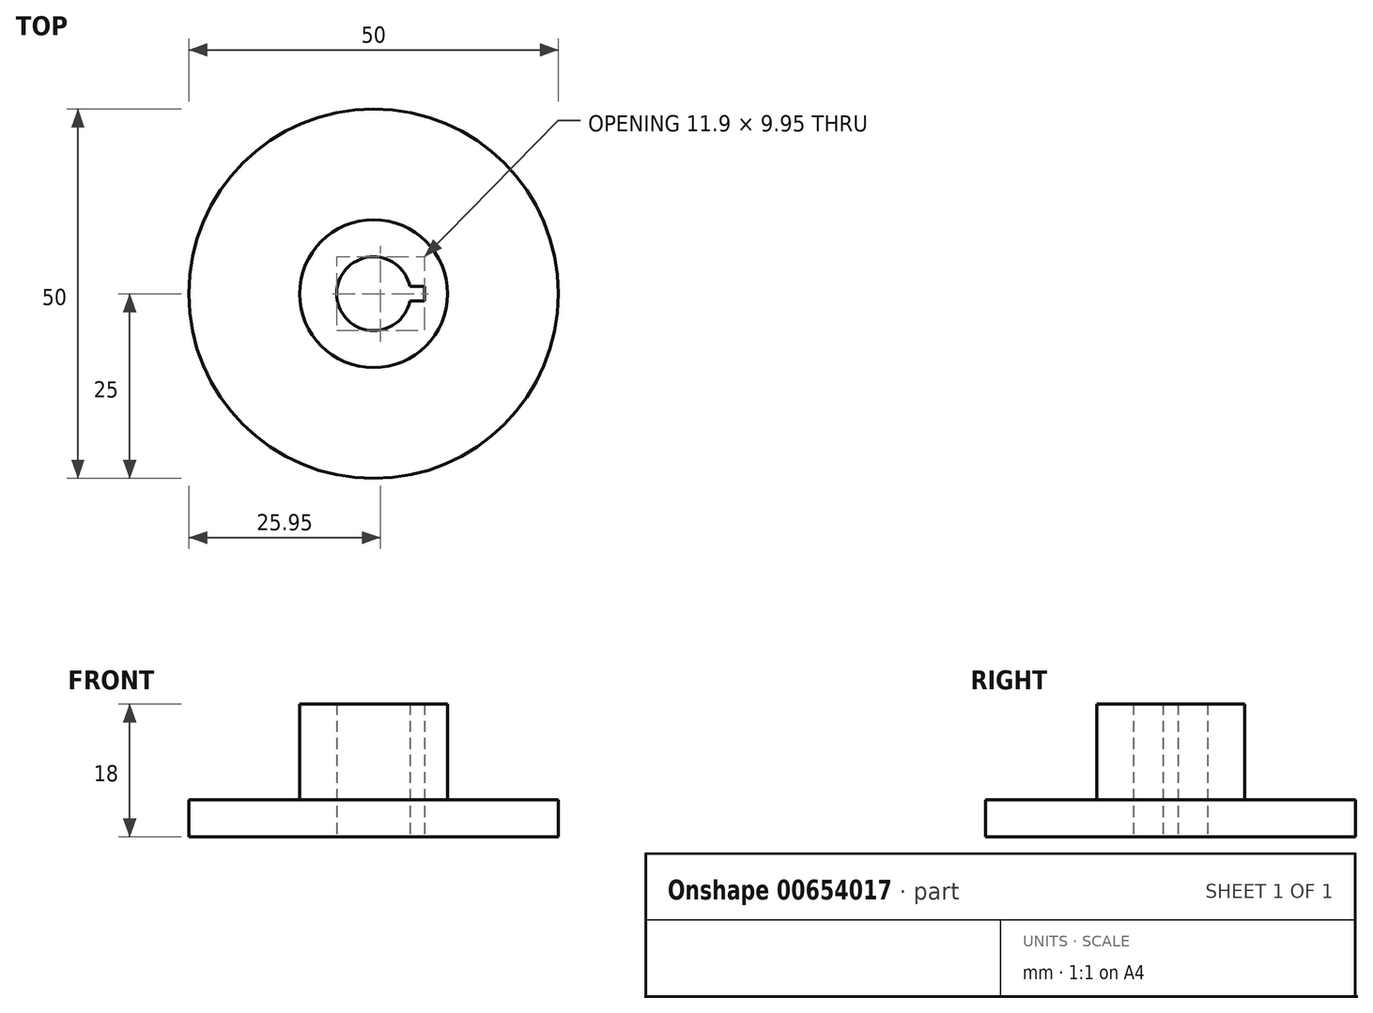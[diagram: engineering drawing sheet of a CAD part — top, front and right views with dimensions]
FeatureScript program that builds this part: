
annotation { "Feature Type Name" : "Feature", "Feature Type Description" : "" }
export const myFeature = defineFeature(function(context is Context, id is Id, definition is map)
    precondition{}
    {
        {
            var Q0;
            Q0=qCreatedBy(makeId("Top.planeOp"),FACE);
            var sketch = newSketch(context, id + "F0", { "sketchPlane" : qUnion([Q0])});
            skCircle(sketch, "E0", {"center": v(0, 0) * mm, "radius": 5 * mm});
            skCircle(sketch, "E1", {"center": v(0, 0) * mm, "radius": 25 * mm});
            skCircle(sketch, "E2", {"center": v(0, 0) * mm, "radius": 10 * mm});
            skLineSegment(sketch, "E3.bottom", {"start": v(6.9, 1) * mm, "end": v(4.9, 1) * mm});
            skLineSegment(sketch, "E3.top", {"start": v(6.9, -1) * mm, "end": v(4.9, -1) * mm});
            skLineSegment(sketch, "E3.left", {"start": v(6.9, 1) * mm, "end": v(6.9, -1) * mm});
            skLineSegment(sketch, "E3.right", {"start": v(4.9, 1) * mm, "end": v(4.9, -1) * mm});
            skPoint(sketch, "E3.middle", {"position": v(5.9, 0) * mm});
            skSolve(sketch);
        }
        {
            var Q0;
            Q0=makeQuery(id+"F0.imprint","IMPRINT",FACE,{"disambiguationData":[TD([[makeQuery(id+"F0.imprint","IMPRINT",EDGE,{"derivedFrom":sQuery(id+"F0.wireOp",EDGE,"E2")}),1.0]])]});
            extrude(context, id + "F1", {"entities" : qUnion([Q0]), "depth" : 18 * mm, "offsetDistance" : 25 * mm});
        }
        {
            var Q0;
            Q0=makeQuery(id+"F0.imprint","IMPRINT",FACE,{"disambiguationData":[TD([[makeQuery(id+"F0.imprint","IMPRINT",EDGE,{"derivedFrom":sQuery(id+"F0.wireOp",EDGE,"E1")}),1.0]])]});
            extrude(context, id + "F2", {"entities" : qUnion([Q0]), "operationType" : NewBodyOperationType.ADD, "depth" : 5 * mm, "offsetDistance" : 25 * mm});
        }
    });
